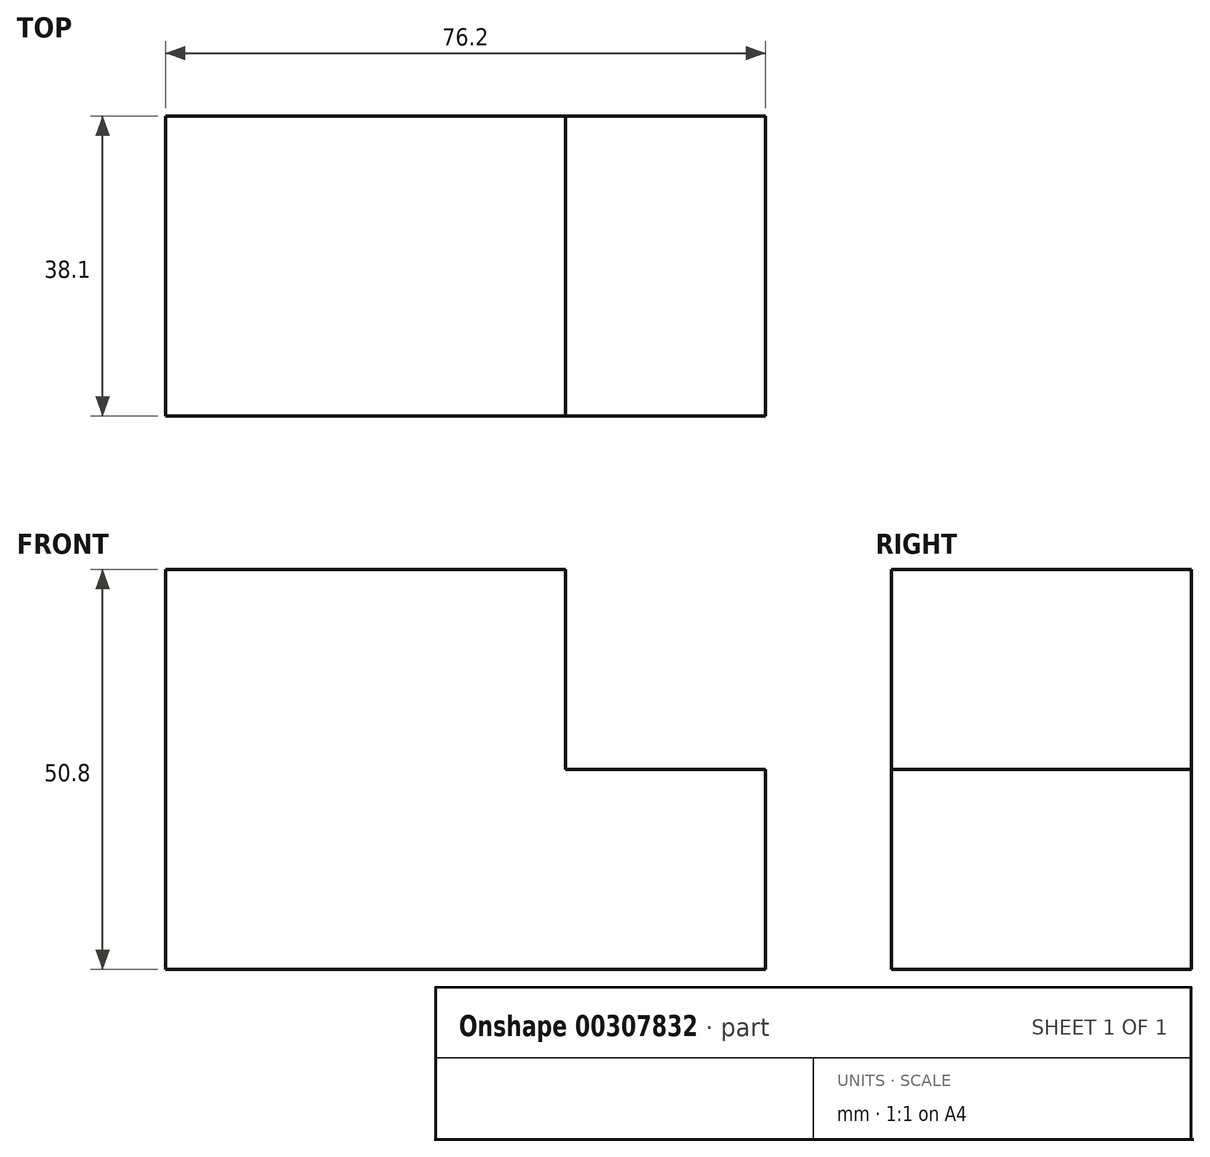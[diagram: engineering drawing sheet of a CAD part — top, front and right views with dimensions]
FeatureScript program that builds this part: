
annotation { "Feature Type Name" : "Feature", "Feature Type Description" : "" }
export const myFeature = defineFeature(function(context is Context, id is Id, definition is map)
    precondition{}
    {
        {
            var Q0;
            Q0=qCreatedBy(makeId("Front.planeOp"),FACE);
            var sketch = newSketch(context, id + "F0", { "sketchPlane" : qUnion([Q0])});
            skLineSegment(sketch, "E0", {"start": v(-27.62, 25.4) * mm, "end": v(23.18, 25.4) * mm});
            skLineSegment(sketch, "E1", {"start": v(23.18, 25.4) * mm, "end": v(23.18, 0) * mm});
            skLineSegment(sketch, "E2", {"start": v(23.18, 0) * mm, "end": v(48.58, 0) * mm});
            skLineSegment(sketch, "E3", {"start": v(48.58, 0) * mm, "end": v(48.58, -25.4) * mm});
            skLineSegment(sketch, "E4", {"start": v(48.58, -25.4) * mm, "end": v(-27.62, -25.4) * mm});
            skLineSegment(sketch, "E5", {"start": v(-27.62, 25.4) * mm, "end": v(-27.62, -25.4) * mm});
            skSolve(sketch);
        }
        {
            var Q0;
            Q0=makeQuery(id+"F0.imprint","IMPRINT",FACE,{"disambiguationData":[TD([[makeQuery(id+"F0.imprint","IMPRINT",EDGE,{"derivedFrom":sQuery(id+"F0.wireOp",EDGE,"E0")}),-1.0]])]});
            extrude(context, id + "F1", {"entities" : qUnion([Q0]), "depth" : 38.1 * mm});
        }
    });
